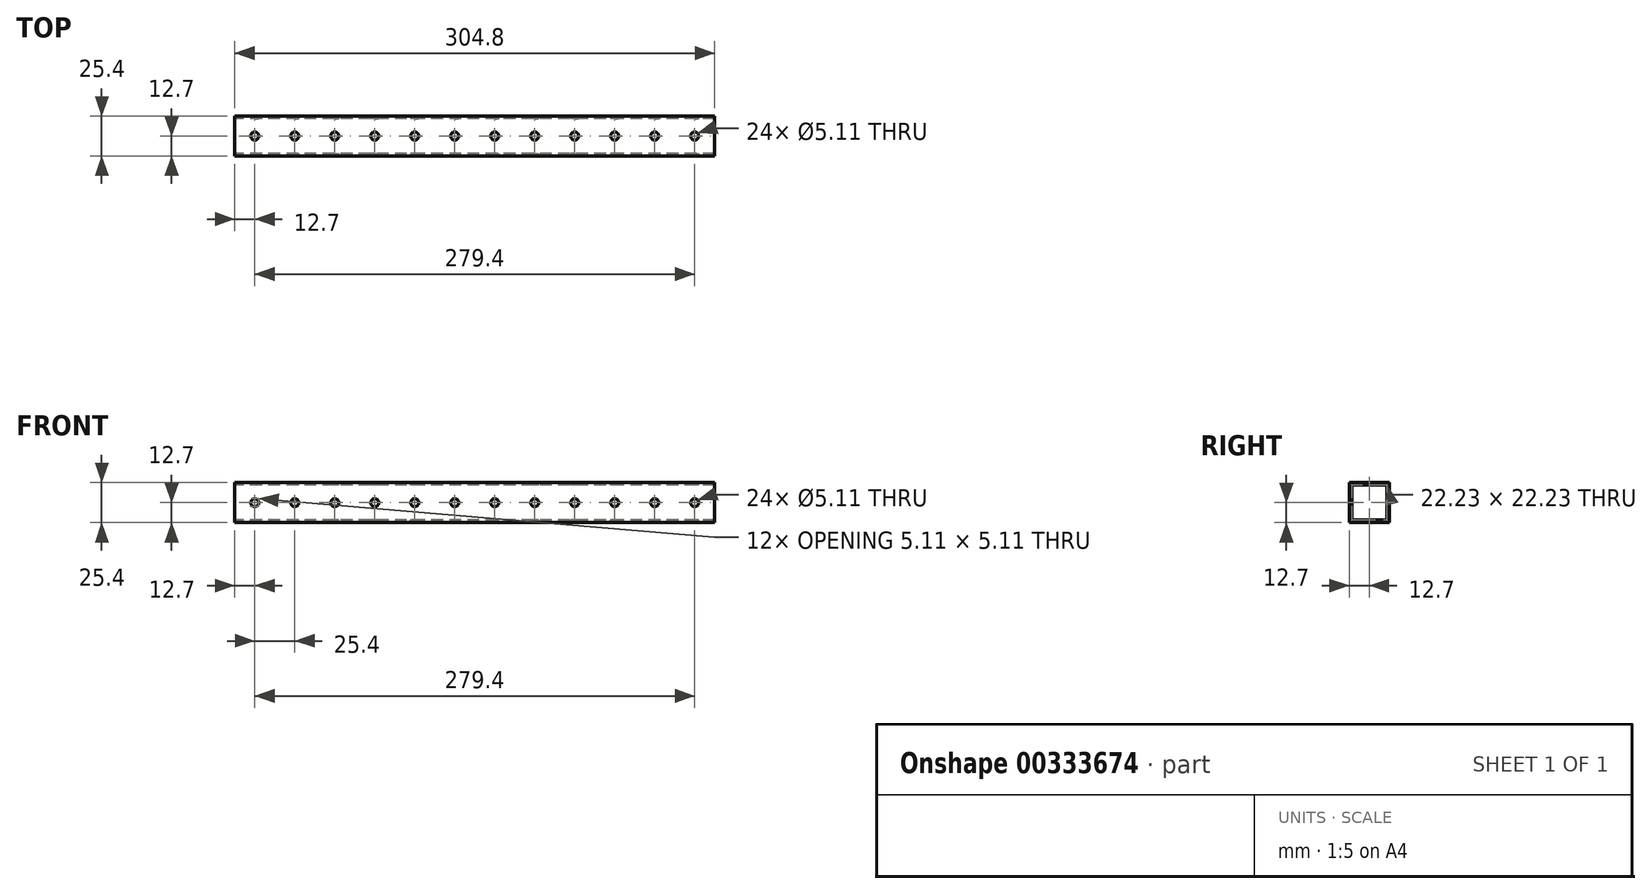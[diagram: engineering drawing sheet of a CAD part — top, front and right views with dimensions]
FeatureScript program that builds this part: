
annotation { "Feature Type Name" : "Feature", "Feature Type Description" : "" }
export const myFeature = defineFeature(function(context is Context, id is Id, definition is map)
    precondition{}
    {
        {
            var Q0;
            Q0=qCreatedBy(makeId("Right.planeOp"),FACE);
            var sketch = newSketch(context, id + "F0", { "sketchPlane" : qUnion([Q0])});
            skLineSegment(sketch, "E0.bottom", {"start": v(12.7, 12.7) * mm, "end": v(-12.7, 12.7) * mm});
            skLineSegment(sketch, "E0.top", {"start": v(12.7, -12.7) * mm, "end": v(-12.7, -12.7) * mm});
            skLineSegment(sketch, "E0.left", {"start": v(12.7, 12.7) * mm, "end": v(12.7, -12.7) * mm});
            skLineSegment(sketch, "E0.right", {"start": v(-12.7, 12.7) * mm, "end": v(-12.7, -12.7) * mm});
            skPoint(sketch, "E0.middle", {"position": v(0, 0) * mm});
            skSolve(sketch);
        }
        {
            var Q0;
            Q0=makeQuery(id+"F0.imprint","IMPRINT",FACE,{"disambiguationData":[TD([[makeQuery(id+"F0.imprint","IMPRINT",EDGE,{"derivedFrom":sQuery(id+"F0.wireOp",EDGE,"E0.bottom")}),1.0]])]});
            extrude(context, id + "F1", {"entities" : qUnion([Q0]), "depth" : 304.8 * mm});
        }
        {
            var Q0;
            Q0=makeQuery(id+"F1.opExtrude","SWEPT_FACE",FACE,{"disambiguationData":[OSD([sQuery(id+"F0.wireOp",EDGE,"E0.right")])]});
            var sketch = newSketch(context, id + "F2", { "sketchPlane" : qUnion([Q0])});
            skCircle(sketch, "E1", {"center": v(12.7, 0) * mm, "radius": 2.55 * mm});
            skCircle(sketch, "E2.1.0.0", {"center": v(38.1, 0) * mm, "radius": 2.55 * mm});
            skCircle(sketch, "E2.2.0.0", {"center": v(63.5, 0) * mm, "radius": 2.55 * mm});
            skCircle(sketch, "E2.3.0.0", {"center": v(88.9, 0) * mm, "radius": 2.55 * mm});
            skCircle(sketch, "E2.4.0.0", {"center": v(114.3, 0) * mm, "radius": 2.55 * mm});
            skCircle(sketch, "E2.5.0.0", {"center": v(139.7, 0) * mm, "radius": 2.55 * mm});
            skCircle(sketch, "E2.6.0.0", {"center": v(165.1, 0) * mm, "radius": 2.55 * mm});
            skCircle(sketch, "E2.7.0.0", {"center": v(190.5, 0) * mm, "radius": 2.55 * mm});
            skCircle(sketch, "E2.8.0.0", {"center": v(215.9, 0) * mm, "radius": 2.55 * mm});
            skCircle(sketch, "E2.9.0.0", {"center": v(241.3, 0) * mm, "radius": 2.55 * mm});
            skCircle(sketch, "E2.10.0.0", {"center": v(266.7, 0) * mm, "radius": 2.55 * mm});
            skCircle(sketch, "E2.11.0.0", {"center": v(292.1, 0) * mm, "radius": 2.55 * mm});
            skLineSegment(sketch, "E2.direction1", {"start": v(12.7, 0) * mm, "end": v(38.1, 0) * mm, "construction": true});
            skSolve(sketch);
        }
        {
            var Q0;
            Q0 = qSketchRegion(id + "F2", true);
            extrude(context, id + "F3", {"entities" : qUnion([Q0]), "operationType" : NewBodyOperationType.REMOVE, "oppositeDirection" : true, "depth" : 25.4 * mm});
        }
        {
            var Q0;
            Q0=makeQuery(id+"F1.opExtrude","CAP_FACE",FACE,{"disambiguationData":[OSD([sQuery(id+"F0.wireOp",EDGE,"E0.bottom"),sQuery(id+"F0.wireOp",EDGE,"E0.top"),sQuery(id+"F0.wireOp",EDGE,"E0.left"),sQuery(id+"F0.wireOp",EDGE,"E0.right")])],"isStart":true});
            var sketch = newSketch(context, id + "F4", { "sketchPlane" : qUnion([Q0])});
            skLineSegment(sketch, "E3.bottom", {"start": v(11.11, 11.11) * mm, "end": v(-11.11, 11.11) * mm});
            skLineSegment(sketch, "E3.top", {"start": v(11.11, -11.11) * mm, "end": v(-11.11, -11.11) * mm});
            skLineSegment(sketch, "E3.left", {"start": v(11.11, 11.11) * mm, "end": v(11.11, -11.11) * mm});
            skLineSegment(sketch, "E3.right", {"start": v(-11.11, 11.11) * mm, "end": v(-11.11, -11.11) * mm});
            skPoint(sketch, "E3.middle", {"position": v(0, 0) * mm});
            skSolve(sketch);
        }
        {
            var Q0;
            Q0=makeQuery(id+"F4.imprint","IMPRINT",FACE,{"disambiguationData":[TD([[makeQuery(id+"F4.imprint","IMPRINT",EDGE,{"derivedFrom":sQuery(id+"F4.wireOp",EDGE,"E3.bottom")}),1.0]])]});
            extrude(context, id + "F5", {"entities" : qUnion([Q0]), "operationType" : NewBodyOperationType.REMOVE, "oppositeDirection" : true, "depth" : 304.8 * mm});
        }
        {
            var Q0;
            Q0=makeQuery(id+"F1.opExtrude","SWEPT_FACE",FACE,{"disambiguationData":[OSD([sQuery(id+"F0.wireOp",EDGE,"E0.bottom")])]});
            var sketch = newSketch(context, id + "F6", { "sketchPlane" : qUnion([Q0])});
            skCircle(sketch, "E4", {"center": v(12.7, 0) * mm, "radius": 2.55 * mm});
            skCircle(sketch, "E5.1.0.0", {"center": v(38.1, 0) * mm, "radius": 2.55 * mm});
            skCircle(sketch, "E5.2.0.0", {"center": v(63.5, 0) * mm, "radius": 2.55 * mm});
            skCircle(sketch, "E5.3.0.0", {"center": v(88.9, 0) * mm, "radius": 2.55 * mm});
            skCircle(sketch, "E5.4.0.0", {"center": v(114.3, 0) * mm, "radius": 2.55 * mm});
            skCircle(sketch, "E5.5.0.0", {"center": v(139.7, 0) * mm, "radius": 2.55 * mm});
            skCircle(sketch, "E5.6.0.0", {"center": v(165.1, 0) * mm, "radius": 2.55 * mm});
            skCircle(sketch, "E5.7.0.0", {"center": v(190.5, 0) * mm, "radius": 2.55 * mm});
            skCircle(sketch, "E5.8.0.0", {"center": v(215.9, 0) * mm, "radius": 2.55 * mm});
            skCircle(sketch, "E5.9.0.0", {"center": v(241.3, 0) * mm, "radius": 2.55 * mm});
            skCircle(sketch, "E5.10.0.0", {"center": v(266.7, 0) * mm, "radius": 2.55 * mm});
            skCircle(sketch, "E5.11.0.0", {"center": v(292.1, 0) * mm, "radius": 2.55 * mm});
            skLineSegment(sketch, "E5.direction1", {"start": v(12.7, 0) * mm, "end": v(38.1, 0) * mm, "construction": true});
            skSolve(sketch);
        }
        {
            var Q0;
            Q0 = qSketchRegion(id + "F6", true);
            extrude(context, id + "F7", {"entities" : qUnion([Q0]), "operationType" : NewBodyOperationType.REMOVE, "oppositeDirection" : true, "depth" : 25.4 * mm});
        }
    });
